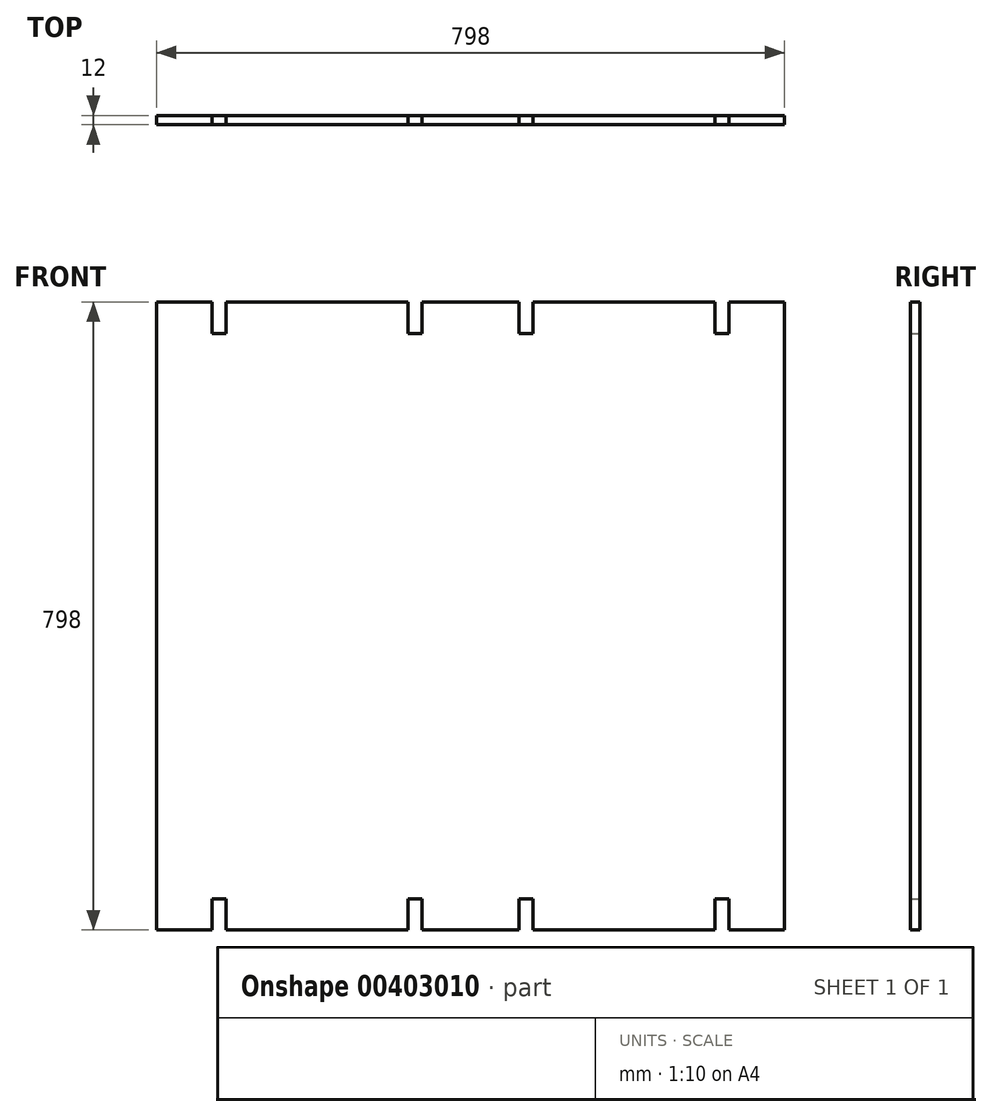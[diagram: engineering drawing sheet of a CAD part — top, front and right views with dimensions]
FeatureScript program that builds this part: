
annotation { "Feature Type Name" : "Feature", "Feature Type Description" : "" }
export const myFeature = defineFeature(function(context is Context, id is Id, definition is map)
    precondition{}
    {
        {
            var Q0;
            Q0=qCreatedBy(makeId("Front.planeOp"),FACE);
            var sketch = newSketch(context, id + "F0", { "sketchPlane" : qUnion([Q0])});
            skLineSegment(sketch, "E0.bottom", {"start": v(0, 0) * mm, "end": v(70.5, 0) * mm});
            skLineSegment(sketch, "E0.top", {"start": v(0, 798) * mm, "end": v(70.5, 798) * mm});
            skLineSegment(sketch, "E0.left", {"start": v(0, 0) * mm, "end": v(0, 798) * mm});
            skLineSegment(sketch, "E0.right", {"start": v(798, 0) * mm, "end": v(798, 798) * mm});
            skLineSegment(sketch, "E1.top", {"start": v(70.5, 40) * mm, "end": v(88.5, 40) * mm});
            skLineSegment(sketch, "E1.left", {"start": v(70.5, 0) * mm, "end": v(70.5, 40) * mm});
            skLineSegment(sketch, "E1.right", {"start": v(88.5, 0) * mm, "end": v(88.5, 40) * mm});
            skLineSegment(sketch, "E2.top", {"start": v(319.5, 40) * mm, "end": v(337.5, 40) * mm});
            skLineSegment(sketch, "E2.left", {"start": v(319.5, 0) * mm, "end": v(319.5, 40) * mm});
            skLineSegment(sketch, "E2.right", {"start": v(337.5, 0) * mm, "end": v(337.5, 40) * mm});
            skLineSegment(sketch, "E3.top", {"start": v(460.5, 40) * mm, "end": v(478.5, 40) * mm});
            skLineSegment(sketch, "E3.left", {"start": v(460.5, 0) * mm, "end": v(460.5, 40) * mm});
            skLineSegment(sketch, "E3.right", {"start": v(478.5, 0) * mm, "end": v(478.5, 40) * mm});
            skLineSegment(sketch, "E4.top", {"start": v(709.5, 40) * mm, "end": v(727.5, 40) * mm});
            skLineSegment(sketch, "E4.left", {"start": v(709.5, 0) * mm, "end": v(709.5, 40) * mm});
            skLineSegment(sketch, "E4.right", {"start": v(727.5, 0) * mm, "end": v(727.5, 40) * mm});
            skLineSegment(sketch, "E5.top", {"start": v(70.5, 758) * mm, "end": v(88.5, 758) * mm});
            skLineSegment(sketch, "E5.left", {"start": v(70.5, 798) * mm, "end": v(70.5, 758) * mm});
            skLineSegment(sketch, "E5.right", {"start": v(88.5, 798) * mm, "end": v(88.5, 758) * mm});
            skLineSegment(sketch, "E6.top", {"start": v(319.5, 758) * mm, "end": v(337.5, 758) * mm});
            skLineSegment(sketch, "E6.left", {"start": v(319.5, 798) * mm, "end": v(319.5, 758) * mm});
            skLineSegment(sketch, "E6.right", {"start": v(337.5, 798) * mm, "end": v(337.5, 758) * mm});
            skLineSegment(sketch, "E7.top", {"start": v(460.5, 758) * mm, "end": v(478.5, 758) * mm});
            skLineSegment(sketch, "E7.left", {"start": v(460.5, 798) * mm, "end": v(460.5, 758) * mm});
            skLineSegment(sketch, "E7.right", {"start": v(478.5, 798) * mm, "end": v(478.5, 758) * mm});
            skLineSegment(sketch, "E8.top", {"start": v(709.5, 758) * mm, "end": v(727.5, 758) * mm});
            skLineSegment(sketch, "E8.left", {"start": v(709.5, 798) * mm, "end": v(709.5, 758) * mm});
            skLineSegment(sketch, "E8.right", {"start": v(727.5, 798) * mm, "end": v(727.5, 758) * mm});
            skLineSegment(sketch, "E9.trimOffspring", {"start": v(88.5, 798) * mm, "end": v(319.5, 798) * mm});
            skLineSegment(sketch, "E10.trimOffspring", {"start": v(337.5, 798) * mm, "end": v(460.5, 798) * mm});
            skLineSegment(sketch, "E11.trimOffspring", {"start": v(478.5, 798) * mm, "end": v(709.5, 798) * mm});
            skLineSegment(sketch, "E12.trimOffspring", {"start": v(727.5, 798) * mm, "end": v(798, 798) * mm});
            skLineSegment(sketch, "E13.trimOffspring", {"start": v(88.5, 0) * mm, "end": v(319.5, 0) * mm});
            skLineSegment(sketch, "E14.trimOffspring", {"start": v(337.5, 0) * mm, "end": v(460.5, 0) * mm});
            skLineSegment(sketch, "E15.trimOffspring", {"start": v(478.5, 0) * mm, "end": v(709.5, 0) * mm});
            skLineSegment(sketch, "E16.trimOffspring", {"start": v(727.5, 0) * mm, "end": v(798, 0) * mm});
            skSolve(sketch);
        }
        {
            var Q0;
            Q0=makeQuery(id+"F0.imprint","IMPRINT",FACE,{"disambiguationData":[TD([[makeQuery(id+"F0.imprint","IMPRINT",EDGE,{"derivedFrom":sQuery(id+"F0.wireOp",EDGE,"ESCJjQW9-Kipg-MWqb-1C1w-8BTgatxLSc3F.bottom")}),1.0]])]});
            var Q1;
            Q1=makeQuery(id+"F0.imprint","IMPRINT",FACE,{"disambiguationData":[TD([[makeQuery(id+"F0.imprint","IMPRINT",EDGE,{"derivedFrom":sQuery(id+"F0.wireOp",EDGE,"E0.bottom")}),1.0]])]});
            extrude(context, id + "F1", {"entities" : qUnion([Q0, Q1]), "depth" : 12 * mm});
        }
    });
